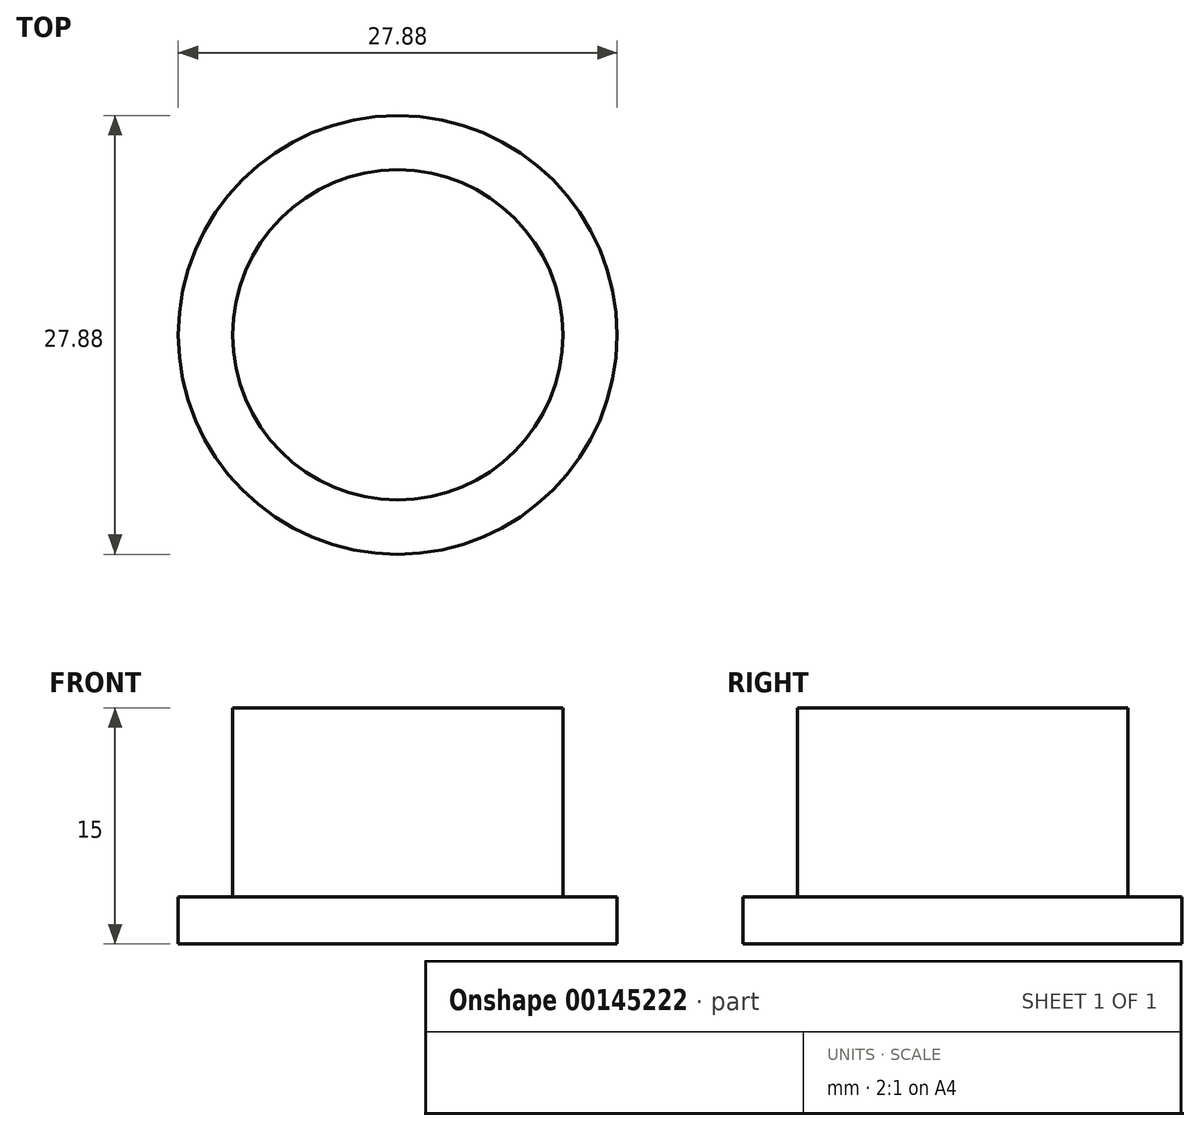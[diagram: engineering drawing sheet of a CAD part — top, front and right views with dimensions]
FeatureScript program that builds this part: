
annotation { "Feature Type Name" : "Feature", "Feature Type Description" : "" }
export const myFeature = defineFeature(function(context is Context, id is Id, definition is map)
    precondition{}
    {
        {
            var Q0;
            Q0=qCreatedBy(makeId("Top.planeOp"),FACE);
            var sketch = newSketch(context, id + "F0", { "sketchPlane" : qUnion([Q0])});
            skCircle(sketch, "E0", {"center": v(0, 0) * mm, "radius": 13.94 * mm});
            skSolve(sketch);
        }
        {
            var Q0;
            Q0=qCreatedBy(makeId("Top.planeOp"),FACE);
            var sketch = newSketch(context, id + "F1", { "sketchPlane" : qUnion([Q0])});
            skCircle(sketch, "E1", {"center": v(0, 0) * mm, "radius": 10.49 * mm});
            skSolve(sketch);
        }
        {
            var Q0;
            Q0 = qSketchRegion(id + "F1", true);
            extrude(context, id + "F2", {"entities" : qUnion([Q0]), "depth" : 15 * mm});
        }
        {
            var Q0;
            Q0=makeQuery(id+"F0.imprint","IMPRINT",FACE,{"disambiguationData":[TD([[makeQuery(id+"F0.imprint","IMPRINT",EDGE,{"derivedFrom":sQuery(id+"F0.wireOp",EDGE,"E0")}),1.0]])]});
            extrude(context, id + "F3", {"entities" : qUnion([Q0]), "operationType" : NewBodyOperationType.ADD, "depth" : 3 * mm});
        }
    });
